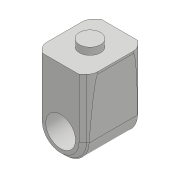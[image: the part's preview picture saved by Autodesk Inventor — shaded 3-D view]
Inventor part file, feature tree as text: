
AUTODESK INVENTOR PART (.ipt)
format: ipt  version: 2018 (Build 220112000, 112)  size: 651,264 bytes
history: native  units: mm
features: sketch x32, projected_geometry x32, extrude x29, fillet x4, hole x3, chamfer x3, mirror x1
ambient origin geometry x8: Origin, YZ Plane, XZ Plane, XY Plane, X Axis, Y Axis, Z Axis, Center Point
bodies: Solid1 (feature_tree)
feature tree (104):
  extrude  "Extrusion1"  Depth=45.0mm
  extrude  "Extrusion2"  Depth=2.25mm
  hole  "Hole1"  [1 undecoded]
  hole  "Hole2"  [1 undecoded]
  fillet  "Fillet1"  Radius=14.0mm
  extrude  "Extrusion3"  Depth=18.5mm
  extrude  "Extrusion4"  Depth=10.0mm
  extrude  "Extrusion5"  Depth=2.195mm
  extrude  "Extrusion6"  Depth=8.0mm
  hole  "Hole3"  [1 undecoded]
  extrude  "Extrusion7"  Depth=8.0mm
  extrude  "Extrusion8"  Depth=5.0mm TaperAngle=0.0deg
  extrude  "Extrusion9"  Depth=10.0mm
  extrude  "Extrusion10"  Depth=10.0mm
  extrude  "Extrusion11"  Depth=14.5mm
  extrude  "Extrusion12"  Depth=14.5mm
  extrude  "Extrusion13"  Depth=5.0mm
  extrude  "Extrusion14"  Depth=5.0mm
  extrude  "Extrusion15"  Depth=5.0mm
  extrude  "Extrusion16"  Depth=5.0mm
  extrude  "Extrusion17"  Depth=4.0mm
  chamfer  "Chamfer1"  Distance=1.0mm
  fillet  "Fillet7"  Radius=20.7mm
  fillet  "Fillet8"  Radius=32.0mm
  mirror  "Mirror1"
  extrude  "Extrusion19"  Depth=5.0mm TaperAngle=0.0deg
  extrude  "Extrusion20"  Depth=8.0mm
  extrude  "Extrusion21"  Depth=0.2mm TaperAngle=0.0deg
  extrude  "Extrusion22"  Depth=0.5mm TaperAngle=0.0deg
  extrude  "Extrusion23"  Depth=5.0mm TaperAngle=0.0deg
  chamfer  "Chamfer2"  Distance=5.0mm
  fillet  "Fillet9"  Radius=0.2mm
  extrude  "Extrusion24"  Depth=2.5mm TaperAngle=45.0deg
  extrude  "Extrusion27"  Depth=0.5mm
  extrude  "Extrusion28"  Depth=1.8mm TaperAngle=0.0deg
  extrude  "Extrusion29"  Depth=5.0mm
  chamfer  "Chamfer4"  Distance=4.2225mm
  extrude  "Extrusion30"  Depth=5.0mm TaperAngle=0.0deg
  extrude  "Extrusion31"  Depth=5.0mm TaperAngle=0.0deg
  extrude  "Extrusion32"  Depth=5.0mm TaperAngle=0.0deg
  sketch  "Sketch1"  dims[d0=24.5mm d1=45.0mm]
  sketch  "Sketch2"  dims[d2=1.95mm d3=0.0mm d4=2.25mm]
  projected_geometry  "Projected Loop1"
  sketch  "Sketch3"  dims[d5=20.0mm d6=2.25mm]
  projected_geometry  "Projected Loop2"
  sketch  "Sketch4"  dims[d7=5.25mm d8=5.25mm d9=14.0mm]
  projected_geometry  "Projected Loop3"
  sketch  "Sketch5"  dims[d10=5.25mm d11=18.5mm]
  projected_geometry  "Projected Loop4"
  sketch  "Sketch6"  dims[d12=10.0mm d13=0.0mm d14=20.5mm]
  projected_geometry  "Projected Loop5"
  sketch  "Sketch7"  dims[d15=2.0mm d16=2.195mm]
  projected_geometry  "Projected Loop6"
  sketch  "Sketch8"  dims[d17=2.0mm]
  projected_geometry  "Projected Loop7"
  sketch  "Sketch9"  dims[d18=2.4mm d19=6.0mm d20=4.4mm d21=2.0mm d22=90.0deg d23=8.0mm d24=20.594885mm d25=20.5mm]
  projected_geometry  "Projected Loop8"
  projected_geometry  "Projected Loop9"
  sketch  "Sketch10"  dims[d26=26.65mm d27=2.0mm]
  projected_geometry  "Projected Loop10"
  projected_geometry  "Projected Loop11"
  sketch  "Sketch11"  dims[d28=2.0mm]
  projected_geometry  "Projected Loop12"
  sketch  "Sketch12"  dims[d29=2.4mm d30=6.0mm d31=4.4mm d32=2.0mm d33=90.0deg d34=8.0mm d35=20.594885mm d36=0.5mm]
  sketch  "Sketch13"  dims[d37=18.0mm d38=5.0mm d39=0.0mm]
  sketch  "Sketch14"  dims[d41=10.0mm d42=0.0mm d43=24.5mm]
  projected_geometry  "Projected Loop13"
  sketch  "Sketch15"  dims[d44=1.15mm d45=0.0mm d46=10.0mm]
  sketch  "Sketch16"  dims[d47=21.0mm d48=14.5mm]
  projected_geometry  "Projected Loop14"
  sketch  "Sketch17"  dims[d49=20.0mm d50=14.5mm]
  projected_geometry  "Projected Loop15"
  sketch  "Sketch18"  dims[d51=24.5mm d52=5.0mm]
  projected_geometry  "Projected Loop16"
  sketch  "Sketch19"  dims[d53=5.0mm d54=2.25mm]
  projected_geometry  "Projected Loop17"
  sketch  "Sketch20"  dims[d55=2.25mm d56=5.0mm]
  projected_geometry  "Projected Loop18"
  sketch  "Sketch25"  dims[d57=5.0mm d58=9.0mm]
  projected_geometry  "Projected Loop22"
  sketch  "Sketch26"  dims[d59=14.75mm d60=4.0mm d61=1.0mm d62=0.0mm d63=20.7mm]
  projected_geometry  "Projected Loop23"
  sketch  "Sketch27"  dims[d64=2.4mm d65=6.0mm d66=4.4mm d67=2.0mm d68=90.0deg d69=8.0mm d70=20.594885mm d72=32.0mm]
  projected_geometry  "Projected Loop25"
  sketch  "Sketch29"  dims[d73=5.0mm d74=0.0mm d75=1.0mm d76=0.0mm]
  projected_geometry  "Projected Loop26"
  sketch  "Sketch30"  dims[d77=12.25mm d78=0.0mm d80=8.0mm]
  projected_geometry  "Projected Loop27"
  sketch  "Sketch32"  dims[d81=4.5mm d82=0.0mm d84=0.2mm d85=0.0mm]
  projected_geometry  "Projected Loop28"
  projected_geometry  "Projected Loop29"
  sketch  "Sketch36"  dims[d86=21.0mm d87=0.5mm d88=0.0mm]
  projected_geometry  "Projected Loop33"
  sketch  "Sketch37"  dims[d91=8.0mm d92=0.0mm d93=5.0mm d94=0.0mm d95=5.0mm d96=0.0mm d98=0.2mm d99=0.0mm]
  projected_geometry  "Projected Loop34"
  sketch  "Sketch41"  dims[d100=0.2mm d101=0.0mm d102=2.5mm d103=2.0mm d104=45.0deg]
  projected_geometry  "Projected Loop36"
  sketch  "Sketch44"  dims[d105=1.5mm d114=0.5mm]
  projected_geometry  "Projected Loop39"
  projected_geometry  "Projected Loop40"
  sketch  "Sketch45"  dims[d128=1.8mm d129=0.0mm d130=1.8mm d131=0.0mm]
  projected_geometry  "Projected Loop41"
  sketch  "Sketch46"  dims[d133=36.055mm d134=4.2225mm d135=4.2225mm d136=2.0mm d137=0.0mm d138=2.0mm d139=0.0mm d140=2.0mm d141=0.0mm d142=5.0mm d143=2.0mm d144=45.0deg d145=8.0mm d147=33.0mm d148=10.0mm d149=0.0mm d161=20.75mm d162=18.0mm d163=25.0mm d164=0.05mm d165=7.0mm d166=0.0mm d167=1.5mm d168=0.0mm d200=15.0mm d201=1.5mm d202=0.0mm d203=1.5mm d204=2.0mm d205=45.0deg d222=10.0mm d223=0.0mm d224=10.0mm d225=0.0mm d226=15.0mm d227=5.0mm d228=0.0mm]
  projected_geometry  "Projected Loop42"
note: 3 required parameter values undecoded (feature->parameter linkage not recoverable at this tier; creation-order binding heuristic only, values carry confidence <= 0.55)
